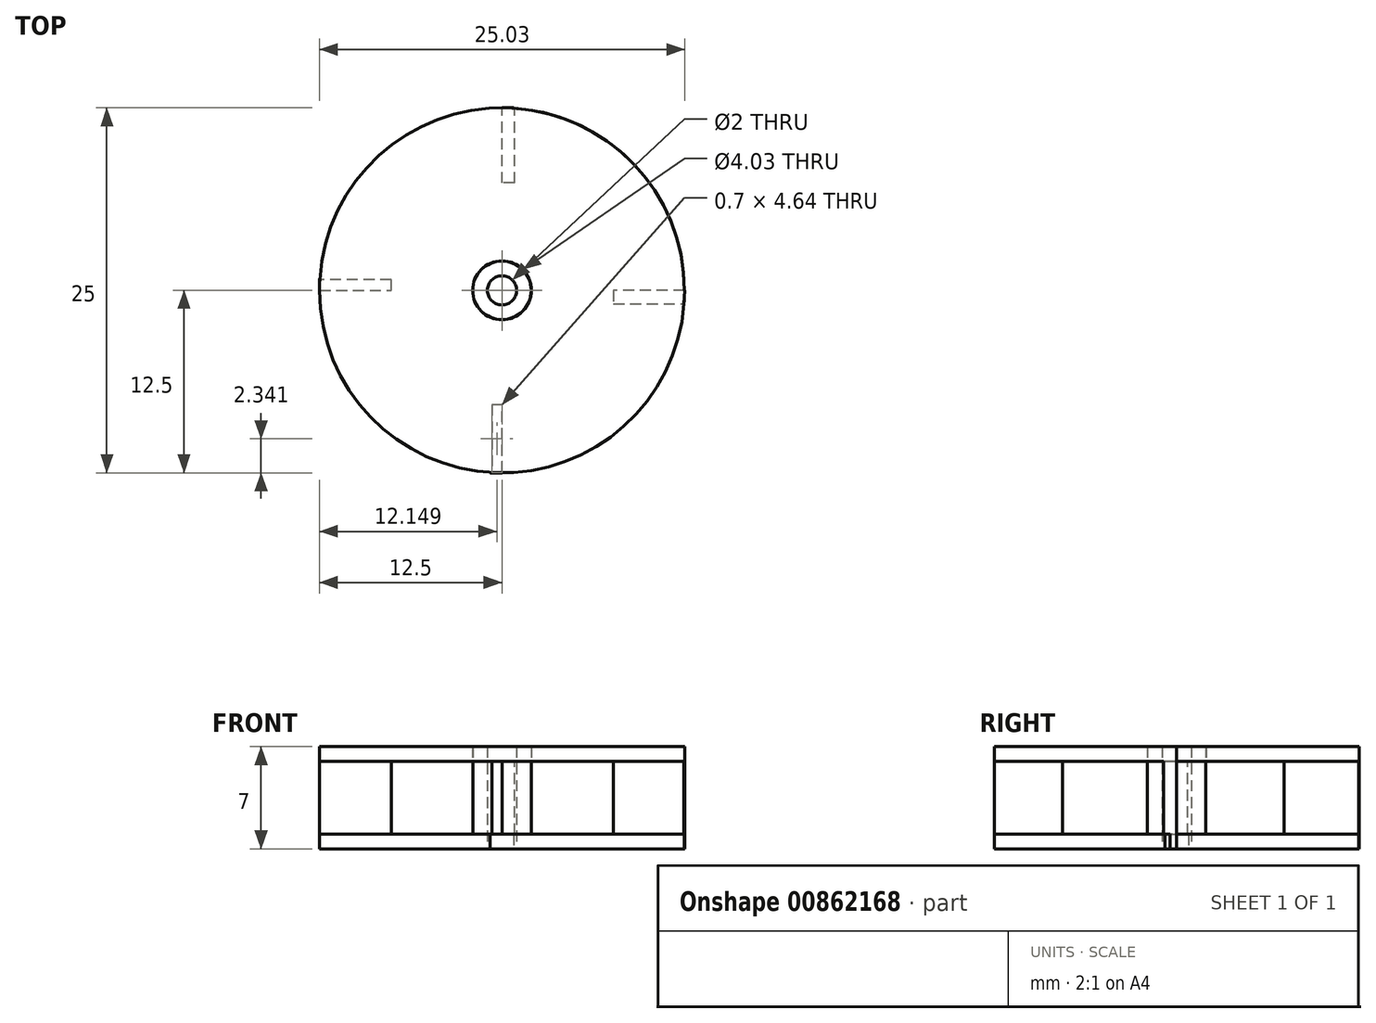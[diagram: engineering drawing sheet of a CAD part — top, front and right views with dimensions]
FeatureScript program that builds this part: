
annotation { "Feature Type Name" : "Feature", "Feature Type Description" : "" }
export const myFeature = defineFeature(function(context is Context, id is Id, definition is map)
    precondition{}
    {
        {
            var Q0;
            Q0=qCreatedBy(makeId("Top.planeOp"),FACE);
            var sketch = newSketch(context, id + "F0", { "sketchPlane" : qUnion([Q0])});
            skCircle(sketch, "E0", {"center": v(0, 0) * mm, "radius": 1 * mm});
            skCircle(sketch, "E1", {"center": v(0, 0) * mm, "radius": 12.5 * mm});
            skCircle(sketch, "E2", {"center": v(0, 0) * mm, "radius": 2 * mm});
            skLineSegment(sketch, "E3", {"start": v(0, 0) * mm, "end": v(0, 2) * mm});
            skLineSegment(sketch, "E4", {"start": v(0, 12.5) * mm, "end": v(0, 7.5) * mm});
            skLineSegment(sketch, "E5", {"start": v(0, -12.5) * mm, "end": v(0, -7.5) * mm});
            skLineSegment(sketch, "E6", {"start": v(0, 0) * mm, "end": v(2, 0) * mm});
            skLineSegment(sketch, "E7", {"start": v(12.5, 0) * mm, "end": v(7.5, 0) * mm});
            skLineSegment(sketch, "E8", {"start": v(0, 0) * mm, "end": v(-2, 0) * mm});
            skLineSegment(sketch, "E9", {"start": v(-12.5, 0) * mm, "end": v(-7.5, 0) * mm});
            skLineSegment(sketch, "E10", {"start": v(0, 0) * mm, "end": v(0, 0) * mm});
            skLineSegment(sketch, "E11", {"start": v(0, 7.5) * mm, "end": v(0.8, 7.5) * mm});
            skLineSegment(sketch, "E12.top", {"start": v(-12.5, 0.8) * mm, "end": v(-7.5, 0.8) * mm});
            skLineSegment(sketch, "E12.left", {"start": v(-12.5, 0) * mm, "end": v(-12.5, 0.8) * mm});
            skLineSegment(sketch, "E12.right", {"start": v(-7.5, 0) * mm, "end": v(-7.5, 0.8) * mm});
            skLineSegment(sketch, "E13.bottom", {"start": v(0, 12.5) * mm, "end": v(0.8, 12.5) * mm});
            skLineSegment(sketch, "E13.right", {"start": v(0.8, 12.5) * mm, "end": v(0.8, 7.5) * mm});
            skLineSegment(sketch, "E14.bottom", {"start": v(11.57, 0) * mm, "end": v(12.5, 0) * mm});
            skLineSegment(sketch, "E14.top", {"start": v(11.57, 0) * mm, "end": v(12.5, 0) * mm});
            skLineSegment(sketch, "E14.left", {"start": v(11.57, 0) * mm, "end": v(11.57, 0) * mm});
            skLineSegment(sketch, "E14.right", {"start": v(12.5, 0) * mm, "end": v(12.5, 0) * mm});
            skLineSegment(sketch, "E15.bottom", {"start": v(12.5, 0) * mm, "end": v(11.57, 0) * mm});
            skLineSegment(sketch, "E15.top", {"start": v(12.5, 0) * mm, "end": v(11.57, 0) * mm});
            skLineSegment(sketch, "E16.top", {"start": v(12.5, -0.8) * mm, "end": v(7.5, -0.8) * mm});
            skLineSegment(sketch, "E16.left", {"start": v(12.5, 0) * mm, "end": v(12.5, -0.8) * mm});
            skLineSegment(sketch, "E16.right", {"start": v(7.5, 0) * mm, "end": v(7.5, -0.8) * mm});
            skLineSegment(sketch, "E17.bottom", {"start": v(0, -12.5) * mm, "end": v(-0.8, -12.5) * mm});
            skLineSegment(sketch, "E17.top", {"start": v(0, -7.5) * mm, "end": v(-0.8, -7.5) * mm});
            skLineSegment(sketch, "E17.right", {"start": v(-0.8, -12.5) * mm, "end": v(-0.8, -7.5) * mm});
            skLineSegment(sketch, "E18.trimOffspring", {"start": v(2, 0) * mm, "end": v(0, 0) * mm});
            skLineSegment(sketch, "E19.trimOffspring", {"start": v(0, 7.5) * mm, "end": v(0, 12.5) * mm});
            skLineSegment(sketch, "E20.trimOffspring", {"start": v(0, 2) * mm, "end": v(0, -2) * mm});
            skLineSegment(sketch, "E21.trimOffspring", {"start": v(7.5, 0) * mm, "end": v(12.5, 0) * mm});
            skLineSegment(sketch, "E22.trimOffspring", {"start": v(0, -7.5) * mm, "end": v(0, -12.5) * mm});
            skLineSegment(sketch, "E23.trimOffspring", {"start": v(0, -2) * mm, "end": v(0, 0) * mm});
            skLineSegment(sketch, "E24.trimOffspring", {"start": v(-7.5, 0) * mm, "end": v(-12.5, 0) * mm});
            skLineSegment(sketch, "E25.trimOffspring", {"start": v(-2, 0) * mm, "end": v(0, 0) * mm});
            skSolve(sketch);
        }
        {
            var Q0;
            Q0 = qSketchRegion(id + "F0", true);
            extrude(context, id + "F1", {"entities" : qUnion([Q0]), "depth" : 1 * mm, "offsetDistance" : 25 * mm});
        }
        {
            var Q0;
            Q0=makeQuery(id+"F0.imprint","IMPRINT",FACE,{"disambiguationData":[TD([[makeQuery(id+"F0.imprint","IMPRINT",EDGE,{"derivedFrom":sQuery(id+"F0.wireOp",EDGE,"E0")}),-1.0]])]});
            extrude(context, id + "F2", {"entities" : qUnion([Q0]), "operationType" : NewBodyOperationType.ADD, "depth" : 6 * mm, "offsetDistance" : 25 * mm});
        }
        {
            var Q0;
            Q0=makeQuery(id+"F2.opExtrude","CAP_FACE",FACE,{"disambiguationData":[OSD([sQuery(id+"F0.wireOp",EDGE,"E0"),sQuery(id+"F0.wireOp",EDGE,"E2")])],"isStart":false});
            var sketch = newSketch(context, id + "F3", { "sketchPlane" : qUnion([Q0])});
            skCircle(sketch, "E26", {"center": v(0, 0) * mm, "radius": 12.5 * mm});
            skCircle(sketch, "E27", {"center": v(0, 0) * mm, "radius": 2.01 * mm});
            skSolve(sketch);
        }
        {
            var Q0;
            Q0=makeQuery(id+"F3.imprint","IMPRINT",FACE,{"disambiguationData":[TD([[makeQuery(id+"F3.imprint","IMPRINT",EDGE,{"derivedFrom":makeQuery(id+"F2.opExtrude","CAP_EDGE",EDGE,{"disambiguationData":[OSD([sQuery(id+"F0.wireOp",EDGE,"E0")])],"isStart":false})}),-1.0]])]});
            var Q1;
            Q1=makeQuery(id+"F3.imprint","IMPRINT",FACE,{"disambiguationData":[TD([[makeQuery(id+"F3.imprint","IMPRINT",EDGE,{"derivedFrom":sQuery(id+"F3.wireOp",EDGE,"E26")}),1.0]])]});
            extrude(context, id + "F4", {"entities" : qUnion([Q0, Q1]), "operationType" : NewBodyOperationType.ADD, "depth" : 1 * mm, "offsetDistance" : 25 * mm});
        }
        {
            var Q0;
            Q0=makeQuery(id+"F4.opExtrude","CAP_FACE",FACE,{"disambiguationData":[OSD([sQuery(id+"F3.wireOp",EDGE,"E26"),sQuery(id+"F3.wireOp",EDGE,"E27")])],"isStart":false});
            var sketch = newSketch(context, id + "F5", { "sketchPlane" : qUnion([Q0])});
            skLineSegment(sketch, "E28", {"start": v(0, -7.84) * mm, "end": v(-0.7, -7.84) * mm});
            skLineSegment(sketch, "E29", {"start": v(-0.7, -7.84) * mm, "end": v(-0.7, -12.48) * mm});
            skLineSegment(sketch, "E30", {"start": v(-0.7, -12.48) * mm, "end": v(0, -12.48) * mm});
            skLineSegment(sketch, "E31", {"start": v(0, -12.48) * mm, "end": v(0, -7.84) * mm});
            skLineSegment(sketch, "E32", {"start": v(0.86, 7.36) * mm, "end": v(0, 7.36) * mm});
            skLineSegment(sketch, "E33", {"start": v(0, 7.36) * mm, "end": v(0, 12.5) * mm});
            skLineSegment(sketch, "E34", {"start": v(0, 12.5) * mm, "end": v(0.86, 12.47) * mm});
            skLineSegment(sketch, "E35", {"start": v(-7.58, 0) * mm, "end": v(-7.58, 0.74) * mm});
            skLineSegment(sketch, "E36", {"start": v(-7.58, 0.74) * mm, "end": v(-12.48, 0.74) * mm});
            skLineSegment(sketch, "E37", {"start": v(-12.48, 0.74) * mm, "end": v(-12.5, 0) * mm});
            skLineSegment(sketch, "E38", {"start": v(-12.5, 0) * mm, "end": v(-7.58, 0) * mm});
            skLineSegment(sketch, "E39", {"start": v(7.63, 0) * mm, "end": v(7.63, -0.9) * mm});
            skLineSegment(sketch, "E40", {"start": v(7.63, -0.9) * mm, "end": v(12.47, -0.9) * mm});
            skLineSegment(sketch, "E41", {"start": v(12.47, -0.9) * mm, "end": v(12.53, 0) * mm});
            skLineSegment(sketch, "E42", {"start": v(12.53, 0) * mm, "end": v(7.63, 0) * mm});
            skLineSegment(sketch, "E43", {"start": v(0.86, 7.36) * mm, "end": v(0.86, 12.47) * mm});
            skSolve(sketch);
        }
        {
            var Q0;
            Q0 = qSketchRegion(id + "F5", true);
            extrude(context, id + "F6", {"entities" : qUnion([Q0]), "operationType" : NewBodyOperationType.ADD, "oppositeDirection" : true, "depth" : 7 * mm, "offsetDistance" : 25 * mm});
        }
    });
